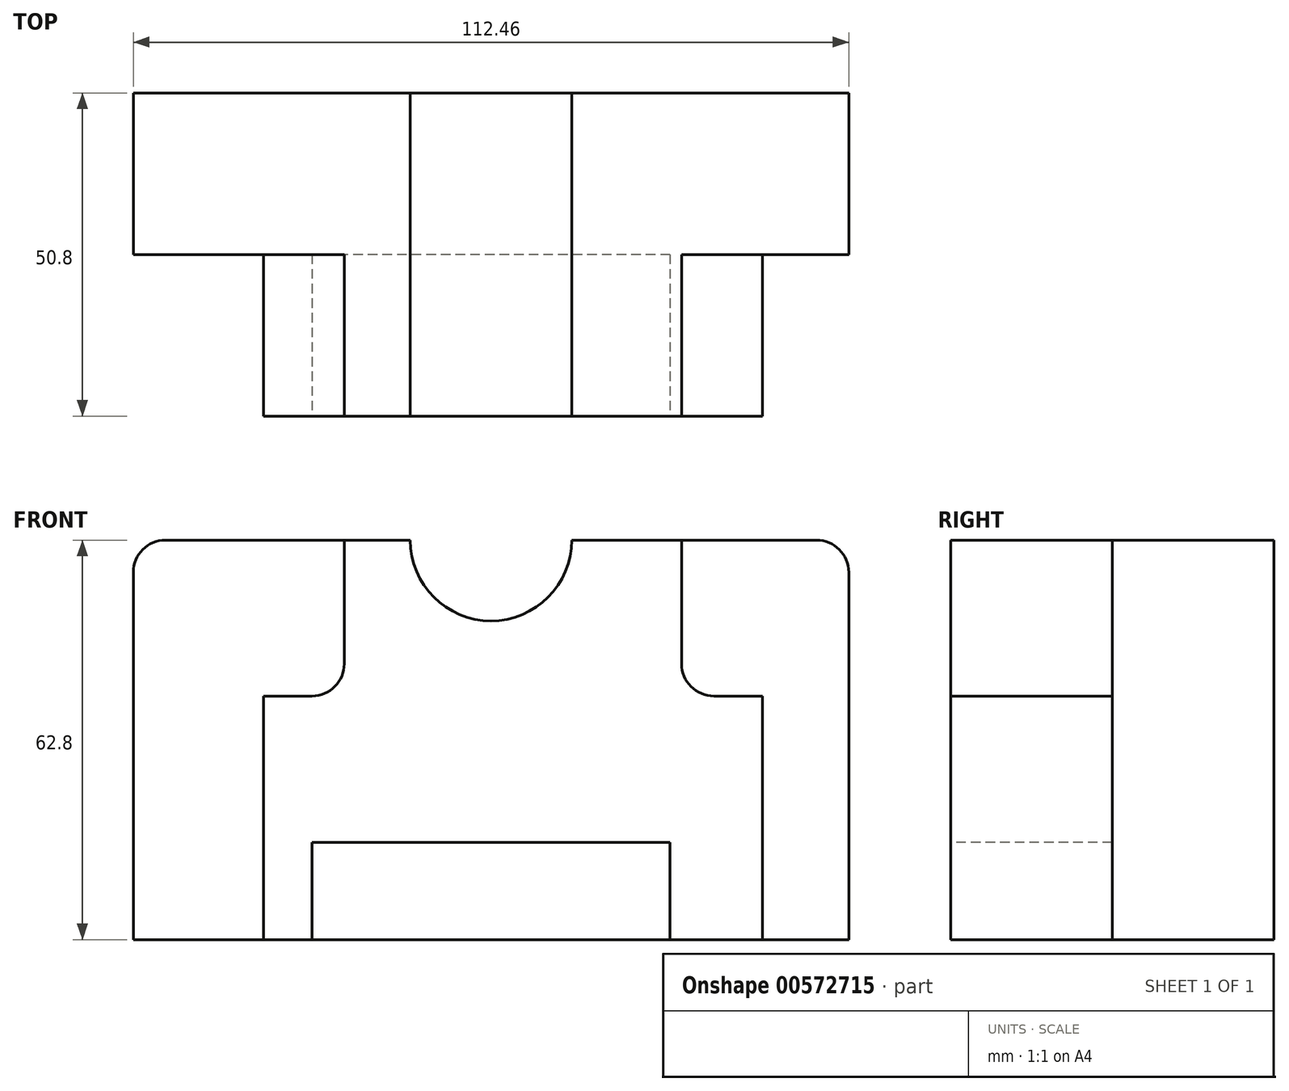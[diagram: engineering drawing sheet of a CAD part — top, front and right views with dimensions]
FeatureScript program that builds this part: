
annotation { "Feature Type Name" : "Feature", "Feature Type Description" : "" }
export const myFeature = defineFeature(function(context is Context, id is Id, definition is map)
    precondition{}
    {
        {
            var Q0;
            Q0=qCreatedBy(makeId("Front.planeOp"),FACE);
            var sketch = newSketch(context, id + "F0", { "sketchPlane" : qUnion([Q0])});
            skLineSegment(sketch, "E0.bottom", {"start": v(56.23, 31.4) * mm, "end": v(-56.23, 31.4) * mm});
            skLineSegment(sketch, "E0.top", {"start": v(56.23, -31.4) * mm, "end": v(-56.23, -31.4) * mm});
            skLineSegment(sketch, "E0.left", {"start": v(56.23, 31.4) * mm, "end": v(56.23, -31.4) * mm});
            skLineSegment(sketch, "E0.right", {"start": v(-56.23, 31.4) * mm, "end": v(-56.23, -31.4) * mm});
            skPoint(sketch, "E0.middle", {"position": v(0, 0) * mm});
            skSolve(sketch);
        }
        {
            var Q0;
            Q0=makeQuery(id+"F0.imprint","IMPRINT",FACE,{"disambiguationData":[TD([[makeQuery(id+"F0.imprint","IMPRINT",EDGE,{"derivedFrom":sQuery(id+"F0.wireOp",EDGE,"E0.bottom")}),1.0]])]});
            extrude(context, id + "F1", {"entities" : qUnion([Q0]), "depth" : 25.4 * mm, "offsetDistance" : 25.4 * mm});
        }
        {
            var Q0;
            Q0=makeQuery(id+"F1.opExtrude","SWEPT_EDGE",EDGE,{"disambiguationData":[OSD([sQuery(id+"F0.wireOp",EDGE,"E0.bottom"),sQuery(id+"F0.wireOp",EDGE,"E0.right")])]});
            var Q1;
            Q1=makeQuery(id+"F1.opExtrude","SWEPT_EDGE",EDGE,{"disambiguationData":[OSD([sQuery(id+"F0.wireOp",EDGE,"E0.bottom"),sQuery(id+"F0.wireOp",EDGE,"E0.left")])]});
            fillet(context, id + "F2", {"entities" : qUnion([Q0, Q1]), "radius" : 5.08 * mm, "tangentPropagation" : true, "allowEdgeOverflow" : false});
        }
        {
            var Q0;
            Q0=makeQuery(id+"F1.opExtrude","CAP_FACE",FACE,{"disambiguationData":[OSD([sQuery(id+"F0.wireOp",EDGE,"E0.bottom"),sQuery(id+"F0.wireOp",EDGE,"E0.top"),sQuery(id+"F0.wireOp",EDGE,"E0.left"),sQuery(id+"F0.wireOp",EDGE,"E0.right")])],"isStart":false});
            var sketch = newSketch(context, id + "F3", { "sketchPlane" : qUnion([Q0])});
            skLineSegment(sketch, "E1.bottom", {"start": v(-35.76, -31.4) * mm, "end": v(42.65, -31.4) * mm});
            skLineSegment(sketch, "E1.top", {"start": v(-35.76, 31.4) * mm, "end": v(42.65, 31.4) * mm});
            skLineSegment(sketch, "E1.left", {"start": v(-35.76, -31.4) * mm, "end": v(-35.76, 31.4) * mm});
            skLineSegment(sketch, "E1.right", {"start": v(42.65, -31.4) * mm, "end": v(42.65, 31.4) * mm});
            skPoint(sketch, "E1.middle", {"position": v(3.45, 0) * mm});
            skSolve(sketch);
        }
        {
            var Q0;
            Q0=makeQuery(id+"F3.imprint","IMPRINT",FACE,{"disambiguationData":[TD([[makeQuery(id+"F3.imprint","IMPRINT",EDGE,{"derivedFrom":sQuery(id+"F3.wireOp",EDGE,"E1.bottom")}),-1.0]])]});
            extrude(context, id + "F4", {"entities" : qUnion([Q0]), "operationType" : NewBodyOperationType.ADD, "depth" : 25.4 * mm, "offsetDistance" : 25.4 * mm});
        }
        {
            var Q0;
            Q0=makeQuery(id+"F4.boolean.opBoolean","MERGE",FACE,{"derivedFrom":[makeQuery(id+"F1.opExtrude","SWEPT_FACE",FACE,{"disambiguationData":[OSD([sQuery(id+"F0.wireOp",EDGE,"E0.bottom")])]}),makeQuery(id+"F4.opExtrude","SWEPT_FACE",FACE,{"disambiguationData":[OSD([sQuery(id+"F3.wireOp",EDGE,"E1.top")])]})]});
            var sketch = newSketch(context, id + "F5", { "sketchPlane" : qUnion([Q0])});
            skLineSegment(sketch, "E2.bottom", {"start": v(0, -50.8) * mm, "end": v(-12.7, -50.8) * mm});
            skLineSegment(sketch, "E2.top", {"start": v(0, 0) * mm, "end": v(-12.7, 0) * mm});
            skLineSegment(sketch, "E2.left", {"start": v(0, -50.8) * mm, "end": v(0, 0) * mm});
            skLineSegment(sketch, "E2.right", {"start": v(-12.7, -50.8) * mm, "end": v(-12.7, 0) * mm});
            skSolve(sketch);
        }
        {
            var Q0;
            Q0=makeQuery(id+"F5.imprint","IMPRINT",FACE,{"disambiguationData":[TD([[makeQuery(id+"F5.imprint","IMPRINT",EDGE,{"derivedFrom":sQuery(id+"F5.wireOp",EDGE,"E2.bottom")}),-1.0]])]});
            var Q1;
            Q1=sQuery(id+"F5.wireOp",EDGE,"E2.left");
            revolve(context, id + "F6", {"operationType" : NewBodyOperationType.REMOVE, "entities" : qUnion([Q0]), "axis" : qUnion([Q1]), "revolveType" : RevolveType.FULL, "oppositeDirection" : true});
        }
        {
            var Q0;
            Q0=makeQuery(id+"F4.opExtrude","CAP_FACE",FACE,{"disambiguationData":[OSD([sQuery(id+"F3.wireOp",EDGE,"E1.bottom"),sQuery(id+"F3.wireOp",EDGE,"E1.top"),sQuery(id+"F3.wireOp",EDGE,"E1.left"),sQuery(id+"F3.wireOp",EDGE,"E1.right")])],"isStart":false});
            var sketch = newSketch(context, id + "F7", { "sketchPlane" : qUnion([Q0])});
            skLineSegment(sketch, "E3.bottom", {"start": v(-28.14, -16.12) * mm, "end": v(28.14, -16.12) * mm});
            skLineSegment(sketch, "E3.top", {"start": v(-28.14, -46.68) * mm, "end": v(28.14, -46.68) * mm});
            skLineSegment(sketch, "E3.left", {"start": v(-28.14, -16.12) * mm, "end": v(-28.14, -46.68) * mm});
            skLineSegment(sketch, "E3.right", {"start": v(28.14, -16.12) * mm, "end": v(28.14, -46.68) * mm});
            skPoint(sketch, "E3.middle", {"position": v(0, -31.4) * mm});
            skPoint(sketch, "E3.middle.positionSnap0", {"position": v(3.45, -31.4) * mm});
            skPoint(sketch, "E3.centerSnap0", {"position": v(3.45, -31.4) * mm});
            skSolve(sketch);
        }
        {
            var Q0;
            {var subQ0=sQuery(id+"F7.wireOp",EDGE,"E3.bottom");Q0=makeQuery(id+"F7.imprint","IMPRINT",FACE,{"disambiguationData":[TD([[makeQuery(id+"F7.imprint","IMPRINT",EDGE,{"derivedFrom":subQ0}),-1.0]])]});}
            extrude(context, id + "F8", {"entities" : qUnion([Q0]), "operationType" : NewBodyOperationType.REMOVE, "oppositeDirection" : true, "depth" : 25.4 * mm, "offsetDistance" : 25.4 * mm});
        }
        {
            var Q0;
            Q0=makeQuery(id+"F4.opExtrude","CAP_FACE",FACE,{"disambiguationData":[OSD([sQuery(id+"F3.wireOp",EDGE,"E1.bottom"),sQuery(id+"F3.wireOp",EDGE,"E1.top"),sQuery(id+"F3.wireOp",EDGE,"E1.left"),sQuery(id+"F3.wireOp",EDGE,"E1.right")])],"isStart":false});
            var sketch = newSketch(context, id + "F9", { "sketchPlane" : qUnion([Q0])});
            skLineSegment(sketch, "E4.bottom", {"start": v(42.65, 31.4) * mm, "end": v(29.95, 31.4) * mm});
            skLineSegment(sketch, "E4.top", {"start": v(42.65, 6.89) * mm, "end": v(29.95, 6.89) * mm});
            skLineSegment(sketch, "E4.left", {"start": v(42.65, 31.4) * mm, "end": v(42.65, 6.89) * mm});
            skLineSegment(sketch, "E4.right", {"start": v(29.95, 31.4) * mm, "end": v(29.95, 6.89) * mm});
            skLineSegment(sketch, "E5.bottom", {"start": v(-35.76, 31.4) * mm, "end": v(-23.06, 31.4) * mm});
            skLineSegment(sketch, "E5.top", {"start": v(-35.76, 6.89) * mm, "end": v(-23.06, 6.89) * mm});
            skLineSegment(sketch, "E5.left", {"start": v(-35.76, 31.4) * mm, "end": v(-35.76, 6.89) * mm});
            skLineSegment(sketch, "E5.right", {"start": v(-23.06, 31.4) * mm, "end": v(-23.06, 6.89) * mm});
            skSolve(sketch);
        }
        {
            var Q0;
            Q0=makeQuery(id+"F9.imprint","IMPRINT",FACE,{"disambiguationData":[TD([[makeQuery(id+"F9.imprint","IMPRINT",EDGE,{"derivedFrom":sQuery(id+"F9.wireOp",EDGE,"E5.bottom")}),1.0]])]});
            var Q1;
            Q1=makeQuery(id+"F9.imprint","IMPRINT",FACE,{"disambiguationData":[TD([[makeQuery(id+"F9.imprint","IMPRINT",EDGE,{"derivedFrom":sQuery(id+"F9.wireOp",EDGE,"E4.bottom")}),1.0]])]});
            extrude(context, id + "F10", {"entities" : qUnion([Q0, Q1]), "operationType" : NewBodyOperationType.REMOVE, "oppositeDirection" : true, "depth" : 25.4 * mm, "offsetDistance" : 25.4 * mm});
        }
        {
            var Q0;
            Q0=makeQuery(id+"F10.boolean.opBoolean","COPY",EDGE,{"derivedFrom":makeQuery(id+"F10.opExtrude","SWEPT_EDGE",EDGE,{"disambiguationData":[OSD([sQuery(id+"F9.wireOp",EDGE,"E5.top"),sQuery(id+"F9.wireOp",EDGE,"E5.right")])]})});
            fillet(context, id + "F11", {"entities" : qUnion([Q0]), "radius" : 5.08 * mm, "tangentPropagation" : true, "allowEdgeOverflow" : false});
        }
        {
            var Q0;
            Q0=makeQuery(id+"F10.boolean.opBoolean","COPY",EDGE,{"derivedFrom":makeQuery(id+"F10.opExtrude","SWEPT_EDGE",EDGE,{"disambiguationData":[OSD([sQuery(id+"F9.wireOp",EDGE,"E4.top"),sQuery(id+"F9.wireOp",EDGE,"E4.right")])]})});
            fillet(context, id + "F12", {"entities" : qUnion([Q0]), "radius" : 5.08 * mm, "tangentPropagation" : true, "allowEdgeOverflow" : false});
        }
    });
